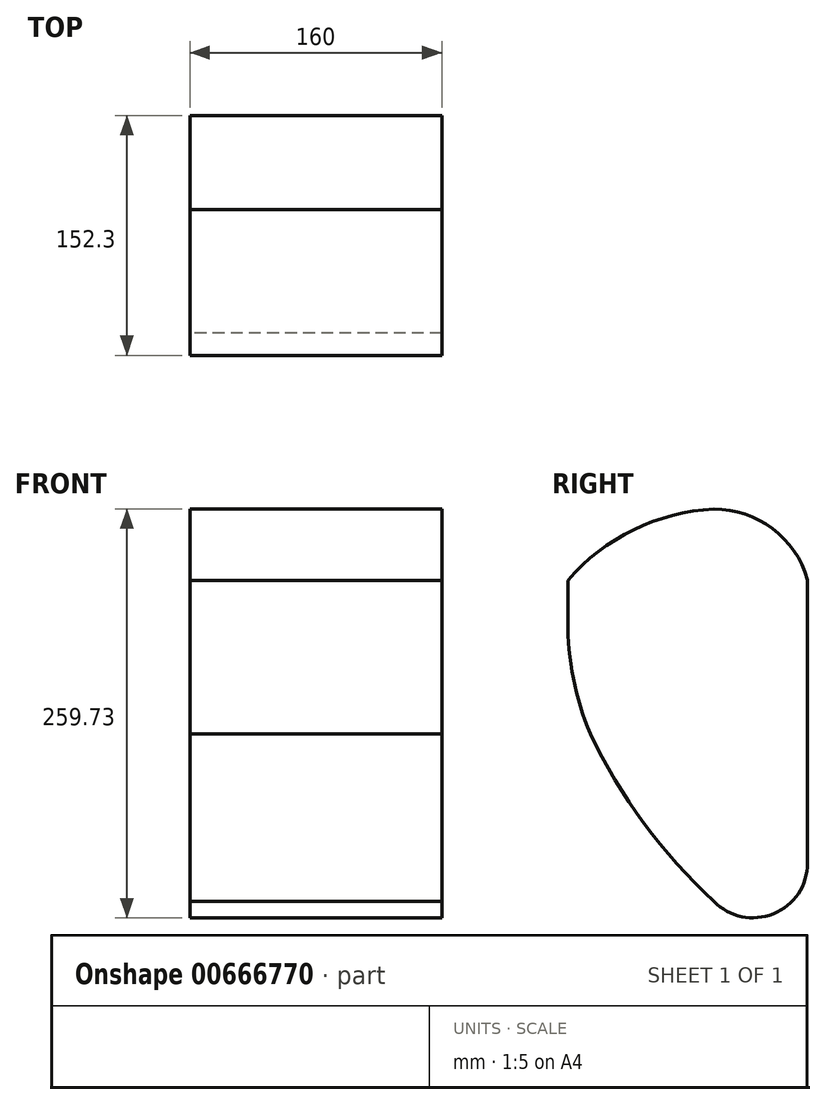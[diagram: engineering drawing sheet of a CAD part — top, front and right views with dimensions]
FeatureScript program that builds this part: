
annotation { "Feature Type Name" : "Feature", "Feature Type Description" : "" }
export const myFeature = defineFeature(function(context is Context, id is Id, definition is map)
    precondition{}
    {
        {
            var Q0;
            Q0=qCreatedBy(makeId("Right.planeOp"),FACE);
            var sketch = newSketch(context, id + "F0", { "sketchPlane" : qUnion([Q0])});
            skLineSegment(sketch, "E0", {"start": v(59.57, 116.48) * mm, "end": v(59.57, -63.52) * mm});
            skArc(sketch, "E1", {"start": v(59.57, 116.48) * mm, "mid": v(37.33, 148.97) * mm, "end": v(0, 161.49) * mm});
            skArc(sketch, "E2", {"start": v(0, -87.77) * mm, "mid": v(37.94, -95.67) * mm, "end": v(59.57, -63.52) * mm});
            skArc(sketch, "E3", {"start": v(0, 161.49) * mm, "mid": v(-50.98, 148.22) * mm, "end": v(-92.73, 116.1) * mm});
            skLineSegment(sketch, "E4", {"start": v(-92.73, 116.1) * mm, "end": v(-92.73, 90.5) * mm});
            skArc(sketch, "E5", {"start": v(-92.73, 90.5) * mm, "mid": v(-89.13, 53.9) * mm, "end": v(-78.47, 18.69) * mm});
            skArc(sketch, "E6", {"start": v(-78.47, 18.69) * mm, "mid": v(-44.22, -38.22) * mm, "end": v(0, -87.77) * mm});
            skSolve(sketch);
        }
        {
            var Q0;
            Q0 = qSketchRegion(id + "F0", true);
            extrude(context, id + "F1", {"entities" : qUnion([Q0]), "depth" : 160 * mm, "offsetDistance" : 25 * mm});
        }
    });
